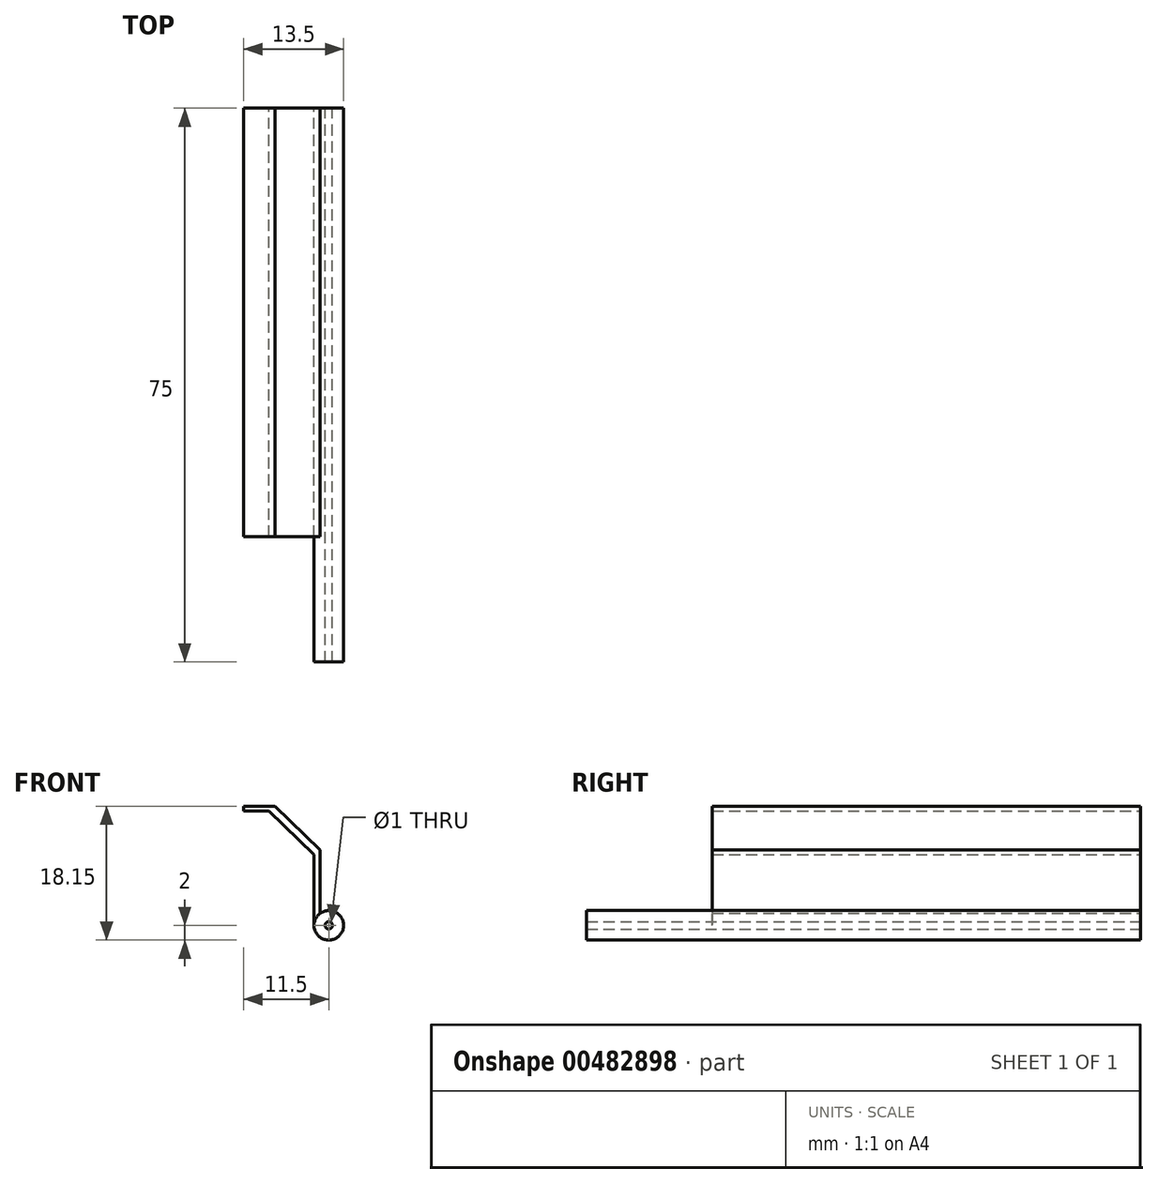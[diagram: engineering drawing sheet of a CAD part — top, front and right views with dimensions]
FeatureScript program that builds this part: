
annotation { "Feature Type Name" : "Feature", "Feature Type Description" : "" }
export const myFeature = defineFeature(function(context is Context, id is Id, definition is map)
    precondition{}
    {
        {
            var Q0;
            Q0=qCreatedBy(makeId("Front.planeOp"),FACE);
            var sketch = newSketch(context, id + "F0", { "sketchPlane" : qUnion([Q0])});
            skLineSegment(sketch, "E0", {"start": v(0, 0) * mm, "end": v(0, 9.6) * mm});
            skLineSegment(sketch, "E1", {"start": v(0, 9.6) * mm, "end": v(-6.12, 15.5) * mm});
            skLineSegment(sketch, "E2", {"start": v(-6.12, 15.5) * mm, "end": v(-9.5, 15.5) * mm});
            skLineSegment(sketch, "E3", {"start": v(-9.5, 15.5) * mm, "end": v(-9.5, 16.15) * mm});
            skLineSegment(sketch, "E4", {"start": v(-9.5, 16.15) * mm, "end": v(-5.28, 16.15) * mm});
            skLineSegment(sketch, "E5", {"start": v(-5.28, 16.15) * mm, "end": v(0.82, 10.21) * mm});
            skLineSegment(sketch, "E6", {"start": v(0.82, 10.21) * mm, "end": v(0.82, 1.62) * mm});
            skCircle(sketch, "E7", {"center": v(2, 0) * mm, "radius": 2 * mm});
            skPoint(sketch, "E8.orphan", {"position": v(0.82, 0) * mm});
            skCircle(sketch, "E9", {"center": v(2, 0) * mm, "radius": 0.5 * mm});
            skSolve(sketch);
        }
        {
            var Q0;
            Q0=makeQuery(id+"F0.imprint","IMPRINT",FACE,{"disambiguationData":[TD([[makeQuery(id+"F0.imprint","IMPRINT",EDGE,{"derivedFrom":sQuery(id+"F0.wireOp",EDGE,"E9")}),-1.0]])]});
            extrude(context, id + "F1", {"entities" : qUnion([Q0]), "depth" : 75 * mm});
        }
        {
            var Q0;
            Q0 = qSketchRegion(id + "F0", true);
            extrude(context, id + "F2", {"entities" : qUnion([Q0]), "operationType" : NewBodyOperationType.ADD, "depth" : 58 * mm});
        }
    });
